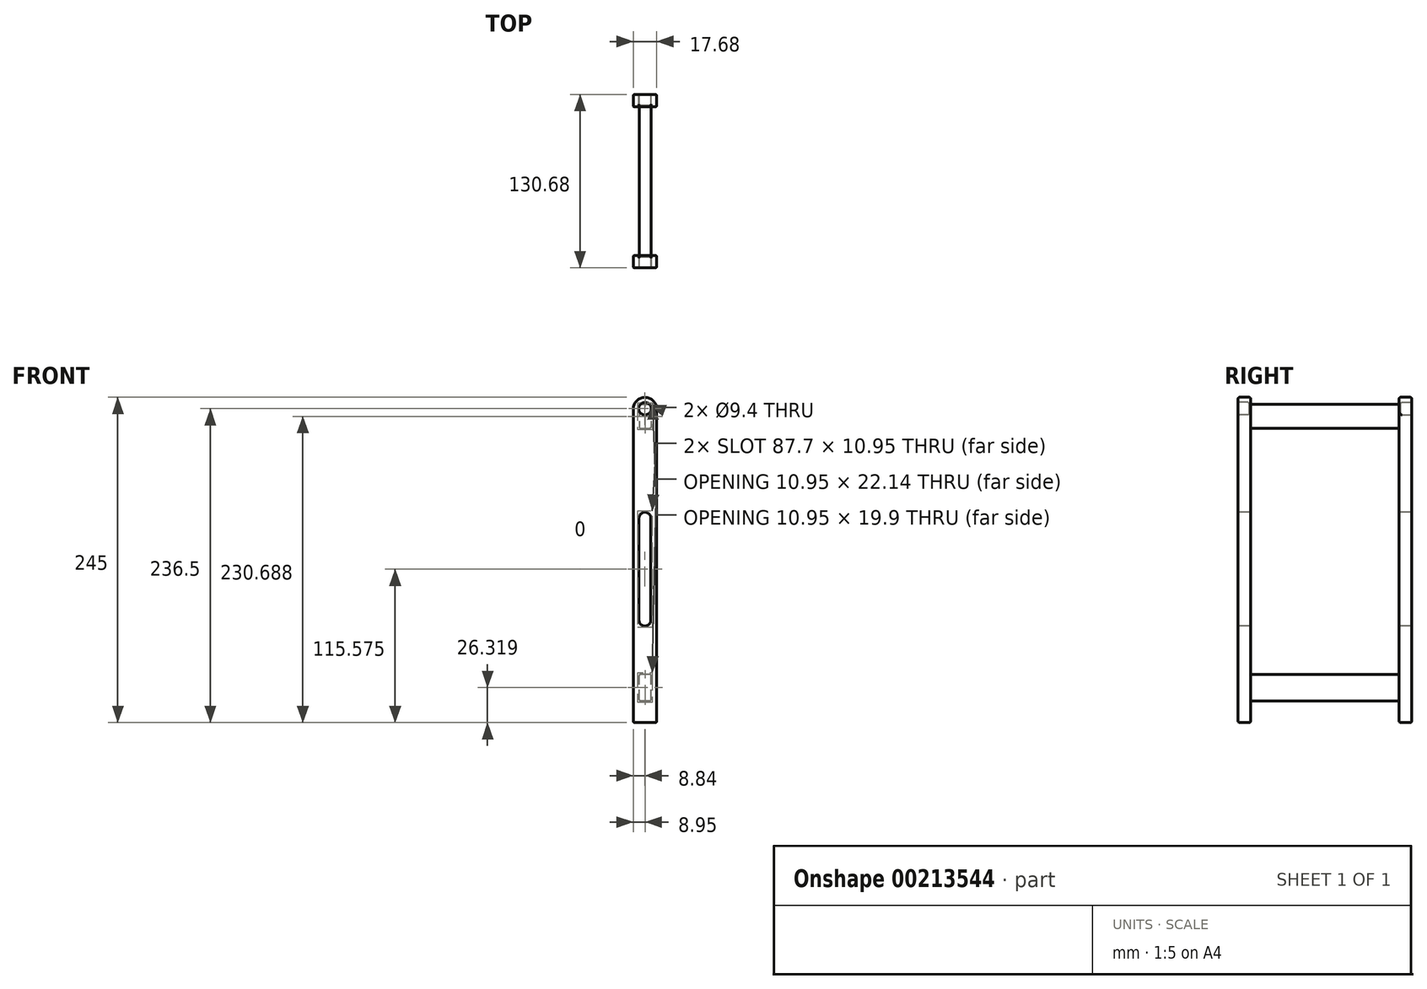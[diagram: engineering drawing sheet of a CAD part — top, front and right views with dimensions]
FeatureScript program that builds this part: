
annotation { "Feature Type Name" : "Feature", "Feature Type Description" : "" }
export const myFeature = defineFeature(function(context is Context, id is Id, definition is map)
    precondition{}
    {
        {
            var Q0;
            Q0=qCreatedBy(makeId("Front.planeOp"),FACE);
            var sketch = newSketch(context, id + "F0", { "sketchPlane" : qUnion([Q0])});
            skLineSegment(sketch, "E0.top", {"start": v(-8.84, -118.08) * mm, "end": v(8.84, -118.08) * mm});
            skLineSegment(sketch, "E0.left", {"start": v(-8.84, 118.08) * mm, "end": v(-8.84, -118.08) * mm});
            skLineSegment(sketch, "E0.right", {"start": v(8.84, 118.08) * mm, "end": v(8.84, -118.08) * mm});
            skPoint(sketch, "E0.middle", {"position": v(0, 0) * mm});
            skArc(sketch, "E1", {"start": v(-8.84, 118.08) * mm, "mid": v(0, 126.92) * mm, "end": v(8.84, 118.08) * mm});
            skSolve(sketch);
        }
        {
            var Q0;
            Q0 = qSketchRegion(id + "F0", true);
            extrude(context, id + "F1", {"entities" : qUnion([Q0]), "depth" : 9.4 * mm});
        }
        {
            var Q0;
            Q0=makeQuery(id+"F1.opExtrude","CAP_FACE",FACE,{"disambiguationData":[OSD([sQuery(id+"F0.wireOp",EDGE,"E0.top"),sQuery(id+"F0.wireOp",EDGE,"E0.left"),sQuery(id+"F0.wireOp",EDGE,"E0.right"),sQuery(id+"F0.wireOp",EDGE,"E1")])],"isStart":false});
            var sketch = newSketch(context, id + "F2", { "sketchPlane" : qUnion([Q0])});
            skLineSegment(sketch, "E2.bottom", {"start": v(4.58, -101.83) * mm, "end": v(-4.37, -101.83) * mm});
            skLineSegment(sketch, "E2.top", {"start": v(4.58, -81.7) * mm, "end": v(-4.37, -81.7) * mm});
            skLineSegment(sketch, "E2.left", {"start": v(4.58, -101.83) * mm, "end": v(4.58, -81.7) * mm});
            skLineSegment(sketch, "E2.right", {"start": v(-4.37, -101.83) * mm, "end": v(-4.37, -81.7) * mm});
            skLineSegment(sketch, "E3.bottom", {"start": v(-4.36, 121.56) * mm, "end": v(4.59, 121.56) * mm});
            skLineSegment(sketch, "E3.top", {"start": v(-4.36, 103.66) * mm, "end": v(4.59, 103.66) * mm});
            skLineSegment(sketch, "E3.left", {"start": v(-4.36, 121.56) * mm, "end": v(-4.36, 103.66) * mm});
            skLineSegment(sketch, "E3.right", {"start": v(4.59, 121.56) * mm, "end": v(4.59, 103.66) * mm});
            skSolve(sketch);
        }
        {
            var Q0;
            Q0=makeQuery(id+"F2.imprint","IMPRINT",FACE,{"disambiguationData":[TD([[makeQuery(id+"F2.imprint","IMPRINT",EDGE,{"derivedFrom":sQuery(id+"F2.wireOp",EDGE,"E3.bottom")}),-1.0]])]});
            var Q1;
            Q1=makeQuery(id+"F2.imprint","IMPRINT",FACE,{"disambiguationData":[TD([[makeQuery(id+"F2.imprint","IMPRINT",EDGE,{"derivedFrom":sQuery(id+"F2.wireOp",EDGE,"E2.bottom")}),-1.0]])]});
            extrude(context, id + "F3", {"entities" : qUnion([Q0, Q1]), "operationType" : NewBodyOperationType.ADD, "depth" : 111.88 * mm});
        }
        {
            var Q0;
            Q0=makeQuery(id+"F3.opExtrude","CAP_FACE",FACE,{"disambiguationData":[OSD([sQuery(id+"F2.wireOp",EDGE,"E3.bottom"),sQuery(id+"F2.wireOp",EDGE,"E3.top"),sQuery(id+"F2.wireOp",EDGE,"E3.left"),sQuery(id+"F2.wireOp",EDGE,"E3.right")])],"isStart":false});
            var sketch = newSketch(context, id + "F4", { "sketchPlane" : qUnion([Q0])});
            skArc(sketch, "E4", {"start": v(8.84, 118.08) * mm, "mid": v(0, 126.92) * mm, "end": v(-8.84, 118.08) * mm});
            skLineSegment(sketch, "E5.bottom", {"start": v(-8.84, -118.08) * mm, "end": v(8.84, -118.08) * mm});
            skLineSegment(sketch, "E5.left", {"start": v(-8.84, -118.08) * mm, "end": v(-8.84, 118.08) * mm});
            skLineSegment(sketch, "E5.right", {"start": v(8.84, -118.08) * mm, "end": v(8.84, 118.08) * mm});
            skSolve(sketch);
        }
        {
            var Q0;
            Q0 = qSketchRegion(id + "F4", true);
            extrude(context, id + "F5", {"entities" : qUnion([Q0]), "operationType" : NewBodyOperationType.ADD, "depth" : 9.4 * mm});
        }
        {
            var Q0;
            Q0=makeQuery(id+"F5.opExtrude","CAP_FACE",FACE,{"disambiguationData":[OSD([sQuery(id+"F4.wireOp",EDGE,"E4"),sQuery(id+"F4.wireOp",EDGE,"E5.bottom"),sQuery(id+"F4.wireOp",EDGE,"E5.left"),sQuery(id+"F4.wireOp",EDGE,"E5.right")])],"isStart":false});
            var sketch = newSketch(context, id + "F6", { "sketchPlane" : qUnion([Q0])});
            skArc(sketch, "E6", {"start": v(4.47, 35.87) * mm, "mid": v(0, 40.34) * mm, "end": v(-4.47, 35.87) * mm});
            skArc(sketch, "E7", {"start": v(-4.47, -40.88) * mm, "mid": v(0, -45.35) * mm, "end": v(4.47, -40.88) * mm});
            skLineSegment(sketch, "E8", {"start": v(-4.47, -40.88) * mm, "end": v(-4.47, 35.87) * mm});
            skLineSegment(sketch, "E9", {"start": v(4.47, 35.87) * mm, "end": v(4.48, -40.88) * mm});
            skCircle(sketch, "E10", {"center": v(0, 118.42) * mm, "radius": 4.7 * mm});
            skLineSegment(sketch, "E11", {"start": v(0, 40.34) * mm, "end": v(0, -45.35) * mm, "construction": true});
            skSolve(sketch);
        }
        {
            var Q0;
            Q0=makeQuery(id+"F6.imprint","IMPRINT",FACE,{"disambiguationData":[TD([[makeQuery(id+"F6.imprint","IMPRINT",EDGE,{"derivedFrom":sQuery(id+"F6.wireOp",EDGE,"E6")}),1.0]])]});
            extrude(context, id + "F7", {"entities" : qUnion([Q0]), "operationType" : NewBodyOperationType.REMOVE, "endBound" : BoundingType.THROUGH_ALL, "oppositeDirection" : true, "depth" : 25 * mm});
        }
        {
            var Q0;
            Q0=makeQuery(id+"F6.imprint","IMPRINT",FACE,{"disambiguationData":[TD([[makeQuery(id+"F6.imprint","IMPRINT",EDGE,{"derivedFrom":sQuery(id+"F6.wireOp",EDGE,"E10")}),1.0]])]});
            extrude(context, id + "F8", {"entities" : qUnion([Q0]), "operationType" : NewBodyOperationType.REMOVE, "oppositeDirection" : true, "depth" : 8.4 * mm});
        }
        {
            var Q0;
            Q0=makeQuery(id+"F1.opExtrude","CAP_FACE",FACE,{"disambiguationData":[OSD([sQuery(id+"F0.wireOp",EDGE,"E0.top"),sQuery(id+"F0.wireOp",EDGE,"E0.left"),sQuery(id+"F0.wireOp",EDGE,"E0.right"),sQuery(id+"F0.wireOp",EDGE,"E1")])],"isStart":true});
            var sketch = newSketch(context, id + "F9", { "sketchPlane" : qUnion([Q0])});
            skCircle(sketch, "E12", {"center": v(0, 118.42) * mm, "radius": 4.7 * mm});
            skSolve(sketch);
        }
        {
            var Q0;
            Q0=makeQuery(id+"F9.imprint","IMPRINT",FACE,{"disambiguationData":[TD([[makeQuery(id+"F9.imprint","IMPRINT",EDGE,{"derivedFrom":sQuery(id+"F9.wireOp",EDGE,"E12")}),1.0]])]});
            extrude(context, id + "F10", {"entities" : qUnion([Q0]), "operationType" : NewBodyOperationType.REMOVE, "oppositeDirection" : true, "depth" : 8.4 * mm});
        }
        {
            var Q0;
            Q0=makeQuery(id+"F5.opExtrude","CAP_FACE",FACE,{"disambiguationData":[OSD([sQuery(id+"F4.wireOp",EDGE,"E4"),sQuery(id+"F4.wireOp",EDGE,"E5.bottom"),sQuery(id+"F4.wireOp",EDGE,"E5.left"),sQuery(id+"F4.wireOp",EDGE,"E5.right")])],"isStart":false});
            var Q1;
            Q1=makeQuery(id+"F1.opExtrude","CAP_FACE",FACE,{"disambiguationData":[OSD([sQuery(id+"F0.wireOp",EDGE,"E0.top"),sQuery(id+"F0.wireOp",EDGE,"E0.left"),sQuery(id+"F0.wireOp",EDGE,"E0.right"),sQuery(id+"F0.wireOp",EDGE,"E1")])],"isStart":false});
            var Q2;
            Q2=makeQuery(id+"F3.opExtrude","SWEPT_FACE",FACE,{"disambiguationData":[OSD([sQuery(id+"F2.wireOp",EDGE,"E3.right")])]});
            var Q3;
            Q3=makeQuery(id+"F3.opExtrude","SWEPT_FACE",FACE,{"disambiguationData":[OSD([sQuery(id+"F2.wireOp",EDGE,"E3.bottom")])]});
            var Q4;
            Q4=makeQuery(id+"F5.opExtrude","CAP_FACE",FACE,{"disambiguationData":[OSD([sQuery(id+"F4.wireOp",EDGE,"E4"),sQuery(id+"F4.wireOp",EDGE,"E5.bottom"),sQuery(id+"F4.wireOp",EDGE,"E5.left"),sQuery(id+"F4.wireOp",EDGE,"E5.right")])],"isStart":true});
            var Q5;
            Q5=makeQuery(id+"F1.opExtrude","CAP_FACE",FACE,{"disambiguationData":[OSD([sQuery(id+"F0.wireOp",EDGE,"E0.top"),sQuery(id+"F0.wireOp",EDGE,"E0.left"),sQuery(id+"F0.wireOp",EDGE,"E0.right"),sQuery(id+"F0.wireOp",EDGE,"E1")])],"isStart":true});
            var Q6;
            Q6=makeQuery(id+"F3.opExtrude","SWEPT_FACE",FACE,{"disambiguationData":[OSD([sQuery(id+"F2.wireOp",EDGE,"E3.left")])]});
            var Q7;
            Q7=makeQuery(id+"F3.opExtrude","SWEPT_EDGE",EDGE,{"disambiguationData":[OSD([sQuery(id+"F2.wireOp",EDGE,"E3.top"),sQuery(id+"F2.wireOp",EDGE,"E3.right")])]});
            var Q8;
            Q8=makeQuery(id+"F3.opExtrude","SWEPT_FACE",FACE,{"disambiguationData":[OSD([sQuery(id+"F2.wireOp",EDGE,"E2.right")])]});
            var Q9;
            Q9=makeQuery(id+"F3.opExtrude","SWEPT_FACE",FACE,{"disambiguationData":[OSD([sQuery(id+"F2.wireOp",EDGE,"E2.left")])]});
            var Q10;
            Q10=makeQuery(id+"F3.opExtrude","SWEPT_FACE",FACE,{"disambiguationData":[OSD([sQuery(id+"F2.wireOp",EDGE,"E2.bottom")])]});
            var Q11;
            Q11=makeQuery(id+"F3.opExtrude","SWEPT_FACE",FACE,{"disambiguationData":[OSD([sQuery(id+"F2.wireOp",EDGE,"E2.top")])]});
            var Q12;
            Q12=makeQuery(id+"F1.opExtrude","SWEPT_FACE",FACE,{"disambiguationData":[OSD([sQuery(id+"F0.wireOp",EDGE,"E0.top")])]});
            var Q13;
            Q13=makeQuery(id+"F5.opExtrude","SWEPT_FACE",FACE,{"disambiguationData":[OSD([sQuery(id+"F4.wireOp",EDGE,"E5.bottom")])]});
            var Q14;
            Q14=makeQuery(id+"F10.boolean.opBoolean","COPY",EDGE,{"derivedFrom":makeQuery(id+"F10.opExtrude","CAP_EDGE",EDGE,{"disambiguationData":[OSD([sQuery(id+"F9.wireOp",EDGE,"E12")])],"isStart":false})});
            var Q15;
            Q15=makeQuery(id+"F8.boolean.opBoolean","COPY",EDGE,{"derivedFrom":makeQuery(id+"F8.opExtrude","CAP_EDGE",EDGE,{"disambiguationData":[OSD([sQuery(id+"F6.wireOp",EDGE,"E10")])],"isStart":false})});
            fillet(context, id + "F11", {"entities" : qUnion([Q0, Q1, Q2, Q3, Q4, Q5, Q6, Q7, Q8, Q9, Q10, Q11, Q12, Q13, Q14, Q15]), "radius" : 1 * mm, "tangentPropagation" : true, "allowEdgeOverflow" : false});
        }
    });
